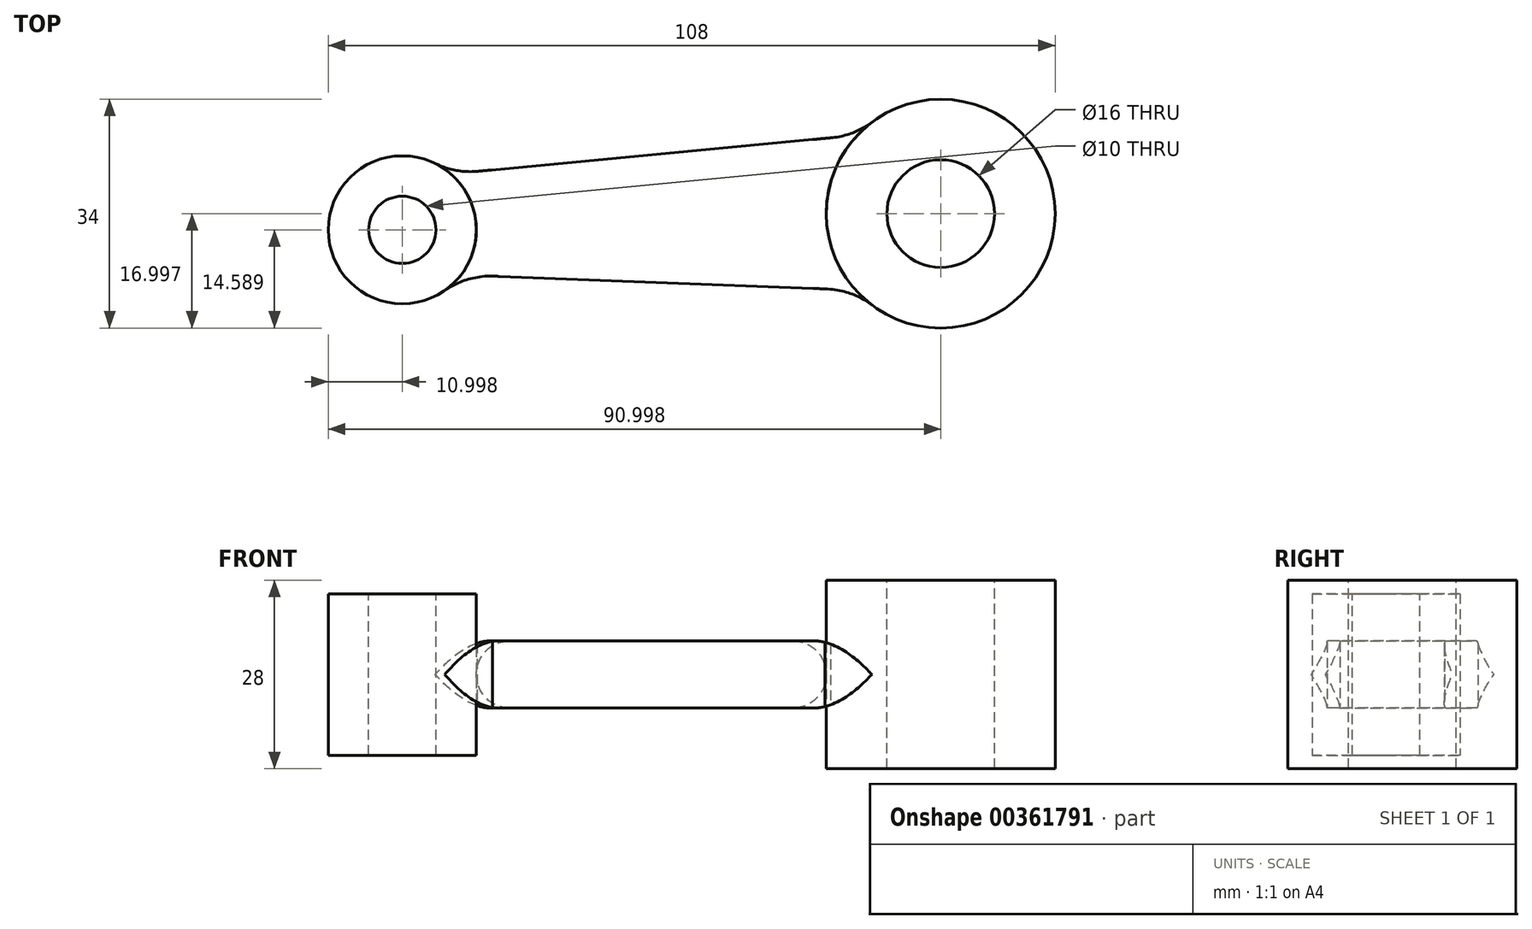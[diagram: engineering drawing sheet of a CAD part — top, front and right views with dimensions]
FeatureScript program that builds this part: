
annotation { "Feature Type Name" : "Feature", "Feature Type Description" : "" }
export const myFeature = defineFeature(function(context is Context, id is Id, definition is map)
    precondition{}
    {
        {
            var Q0;
            Q0=qCreatedBy(makeId("Top.planeOp"),FACE);
            var sketch = newSketch(context, id + "F0", { "sketchPlane" : qUnion([Q0])});
            skArc(sketch, "E0", {"start": v(-38.68, 10.78) * mm, "mid": v(-54.5, 0.06) * mm, "end": v(-37.24, -8.13) * mm});
            skArc(sketch, "E1", {"start": v(26.27, -10.28) * mm, "mid": v(53.48, 3.29) * mm, "end": v(26.3, 16.92) * mm});
            skPoint(sketch, "E2.visualSharp", {"position": v(-36.39, 9.27) * mm});
            skArc(sketch, "E2.filletArc", {"start": v(-38.68, 10.78) * mm, "mid": v(-35.64, 9.76) * mm, "end": v(-32.44, 9.6) * mm});
            skPoint(sketch, "E3.visualSharp", {"position": v(-34.88, -5.9) * mm});
            skArc(sketch, "E3.filletArc", {"start": v(-30.11, -5.98) * mm, "mid": v(-33.85, -6.49) * mm, "end": v(-37.24, -8.13) * mm});
            skPoint(sketch, "E4.visualSharp", {"position": v(24.03, 14.89) * mm});
            skArc(sketch, "E4.filletArc", {"start": v(20.07, 14.57) * mm, "mid": v(23.35, 15.3) * mm, "end": v(26.3, 16.92) * mm});
            skPoint(sketch, "E5.visualSharp", {"position": v(23.72, -7.93) * mm});
            skArc(sketch, "E5.filletArc", {"start": v(26.27, -10.28) * mm, "mid": v(22.98, -8.54) * mm, "end": v(19.3, -7.88) * mm});
            skArc(sketch, "E6", {"start": v(-37.24, -8.13) * mm, "mid": v(-32.55, 1.74) * mm, "end": v(-38.68, 10.78) * mm});
            skArc(sketch, "E7", {"start": v(26.3, 16.92) * mm, "mid": v(19.48, 3.33) * mm, "end": v(26.27, -10.28) * mm});
            skLineSegment(sketch, "E8", {"start": v(-32.44, 9.6) * mm, "end": v(20.07, 14.57) * mm});
            skLineSegment(sketch, "E9", {"start": v(-30.11, -5.98) * mm, "end": v(19.3, -7.88) * mm});
            skSolve(sketch);
        }
        {
            var Q0;
            Q0=makeQuery(id+"F0.imprint","IMPRINT",FACE,{"disambiguationData":[TD([[makeQuery(id+"F0.imprint","IMPRINT",EDGE,{"derivedFrom":sQuery(id+"F0.wireOp",EDGE,"E0")}),1.0]])]});
            extrude(context, id + "F1", {"entities" : qUnion([Q0]), "endBound" : BoundingType.SYMMETRIC, "depth" : 24 * mm});
        }
        {
            var Q0;
            Q0=makeQuery(id+"F0.imprint","IMPRINT",FACE,{"disambiguationData":[TD([[makeQuery(id+"F0.imprint","IMPRINT",EDGE,{"derivedFrom":sQuery(id+"F0.wireOp",EDGE,"E1")}),1.0]])]});
            extrude(context, id + "F2", {"entities" : qUnion([Q0]), "endBound" : BoundingType.SYMMETRIC, "depth" : 28 * mm});
        }
        {
            var Q0;
            Q0=makeQuery(id+"F0.imprint","IMPRINT",FACE,{"disambiguationData":[TD([[makeQuery(id+"F0.imprint","IMPRINT",EDGE,{"derivedFrom":sQuery(id+"F0.wireOp",EDGE,"E2.filletArc")}),-1.0]])]});
            extrude(context, id + "F3", {"entities" : qUnion([Q0]), "endBound" : BoundingType.SYMMETRIC, "depth" : 10 * mm});
        }
        {
            var Q0;
            Q0=makeQuery(id+"F1.opExtrude","CAP_FACE",FACE,{"disambiguationData":[OSD([sQuery(id+"F0.wireOp",EDGE,"E0"),sQuery(id+"F0.wireOp",EDGE,"E6")])],"isStart":false});
            var sketch = newSketch(context, id + "F4", { "sketchPlane" : qUnion([Q0])});
            skCircle(sketch, "E10", {"center": v(-43.52, 0.9) * mm, "radius": 5 * mm});
            skSolve(sketch);
        }
        {
            var Q0;
            Q0=makeQuery(id+"F4.imprint","IMPRINT",FACE,{"disambiguationData":[TD([[makeQuery(id+"F4.imprint","IMPRINT",EDGE,{"derivedFrom":sQuery(id+"F4.wireOp",EDGE,"E10")}),1.0]])]});
            extrude(context, id + "F5", {"entities" : qUnion([Q0]), "operationType" : NewBodyOperationType.REMOVE, "endBound" : BoundingType.THROUGH_ALL, "oppositeDirection" : true, "depth" : 25 * mm});
        }
        {
            var Q0;
            Q0=makeQuery(id+"F2.opExtrude","CAP_FACE",FACE,{"disambiguationData":[OSD([sQuery(id+"F0.wireOp",EDGE,"E1"),sQuery(id+"F0.wireOp",EDGE,"E7")])],"isStart":false});
            var sketch = newSketch(context, id + "F6", { "sketchPlane" : qUnion([Q0])});
            skCircle(sketch, "E11", {"center": v(36.48, 3.3) * mm, "radius": 8 * mm});
            skSolve(sketch);
        }
        {
            var Q0;
            Q0=makeQuery(id+"F6.imprint","IMPRINT",FACE,{"disambiguationData":[TD([[makeQuery(id+"F6.imprint","IMPRINT",EDGE,{"derivedFrom":sQuery(id+"F6.wireOp",EDGE,"E11")}),1.0]])]});
            extrude(context, id + "F7", {"entities" : qUnion([Q0]), "operationType" : NewBodyOperationType.REMOVE, "endBound" : BoundingType.THROUGH_ALL, "oppositeDirection" : true, "depth" : 25 * mm});
        }
        {
            var Q0;
            Q0=makeQuery(id+"F3.opExtrude","CAP_EDGE",EDGE,{"disambiguationData":[OSD([sQuery(id+"F0.wireOp",EDGE,"E6")])],"isStart":false});
            fillet(context, id + "F8", {"entities" : qUnion([Q0]), "radius" : 5 * mm, "tangentPropagation" : true, "allowEdgeOverflow" : false});
        }
        {
            var Q0;
            Q0=makeQuery(id+"F3.opExtrude","CAP_EDGE",EDGE,{"disambiguationData":[OSD([sQuery(id+"F0.wireOp",EDGE,"E6")])],"isStart":true});
            fillet(context, id + "F9", {"entities" : qUnion([Q0]), "radius" : 5 * mm, "tangentPropagation" : true, "allowEdgeOverflow" : false});
        }
        {
            var Q0;
            Q0=makeQuery(id+"F3.opExtrude","CAP_EDGE",EDGE,{"disambiguationData":[OSD([sQuery(id+"F0.wireOp",EDGE,"E7")])],"isStart":true});
            fillet(context, id + "F10", {"entities" : qUnion([Q0]), "radius" : 5 * mm, "tangentPropagation" : true, "allowEdgeOverflow" : false});
        }
        {
            var Q0;
            Q0=makeQuery(id+"F3.opExtrude","CAP_EDGE",EDGE,{"disambiguationData":[OSD([sQuery(id+"F0.wireOp",EDGE,"E7")])],"isStart":false});
            fillet(context, id + "F11", {"entities" : qUnion([Q0]), "radius" : 5 * mm, "tangentPropagation" : true, "allowEdgeOverflow" : false});
        }
    });
